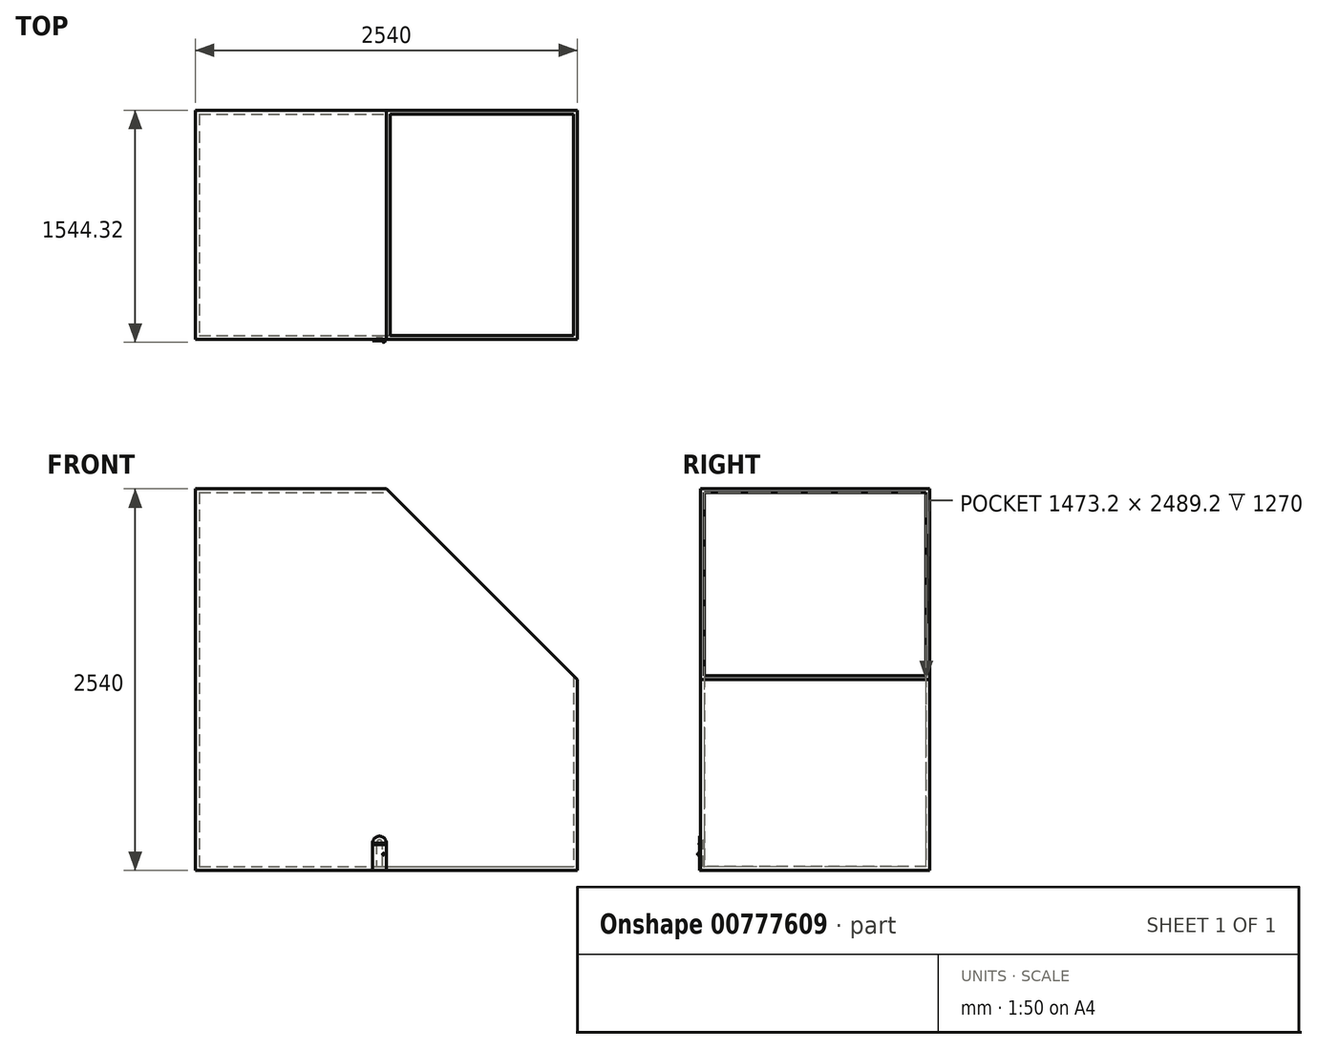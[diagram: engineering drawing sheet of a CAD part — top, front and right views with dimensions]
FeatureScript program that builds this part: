
annotation { "Feature Type Name" : "Feature", "Feature Type Description" : "" }
export const myFeature = defineFeature(function(context is Context, id is Id, definition is map)
    precondition{}
    {
        {
            var Q0;
            Q0=qCreatedBy(makeId("Top.planeOp"),FACE);
            var sketch = newSketch(context, id + "F0", { "sketchPlane" : qUnion([Q0])});
            skLineSegment(sketch, "E0.bottom", {"start": v(-1145.39, 766.67) * mm, "end": v(1394.61, 766.67) * mm});
            skLineSegment(sketch, "E0.top", {"start": v(-1145.39, -757.33) * mm, "end": v(1394.61, -757.33) * mm});
            skLineSegment(sketch, "E0.left", {"start": v(-1145.39, 766.67) * mm, "end": v(-1145.39, -757.33) * mm});
            skLineSegment(sketch, "E0.right", {"start": v(1394.61, 766.67) * mm, "end": v(1394.61, -757.33) * mm});
            skSolve(sketch);
        }
        {
            var Q0;
            Q0 = qSketchRegion(id + "F0", true);
            extrude(context, id + "F1", {"entities" : qUnion([Q0]), "depth" : 2540 * mm, "offsetDistance" : 25.4 * mm});
        }
        {
            var Q0;
            Q0=makeQuery(id+"F1.opExtrude","SWEPT_FACE",FACE,{"disambiguationData":[OSD([sQuery(id+"F0.wireOp",EDGE,"E0.top")])]});
            var sketch = newSketch(context, id + "F2", { "sketchPlane" : qUnion([Q0])});
            skLineSegment(sketch, "E1", {"start": v(124.61, 2540) * mm, "end": v(-1145.39, 1270) * mm});
            skLineSegment(sketch, "E2", {"start": v(-1145.39, 1270) * mm, "end": v(124.61, 2540) * mm});
            skLineSegment(sketch, "E3", {"start": v(124.61, 2540) * mm, "end": v(1394.61, 1270) * mm});
            skSolve(sketch);
        }
        {
            var Q0;
            Q0 = qSketchRegion(id + "F2", true);
            var Q1;
            {var subQ0=sQuery(id+"F2.wireOp",EDGE,"E2");Q1=makeQuery(id+"F2.imprint","IMPRINT",FACE,{"disambiguationData":[TD([[makeQuery(id+"F2.imprint","IMPRINT",EDGE,{"derivedFrom":subQ0}),1.0]])]});}
            var Q2;
            {var subQ0=sQuery(id+"F2.wireOp",EDGE,"E3");Q2=makeQuery(id+"F2.imprint","IMPRINT",FACE,{"disambiguationData":[TD([[makeQuery(id+"F2.imprint","IMPRINT",EDGE,{"derivedFrom":subQ0}),1.0]])]});}
            extrude(context, id + "F3", {"entities" : qUnion([Q0, Q1, Q2]), "operationType" : NewBodyOperationType.REMOVE, "oppositeDirection" : true, "depth" : 2540 * mm, "offsetDistance" : 25.4 * mm});
        }
        {
            var Q0;
            Q0=makeQuery(id+"F1.opExtrude","SWEPT_FACE",FACE,{"disambiguationData":[OSD([sQuery(id+"F0.wireOp",EDGE,"E0.top")])]});
            var sketch = newSketch(context, id + "F4", { "sketchPlane" : qUnion([Q0])});
            skLineSegment(sketch, "E4", {"start": v(1394.61, 0) * mm, "end": v(124.61, 0) * mm});
            skLineSegment(sketch, "E5", {"start": v(124.61, 0) * mm, "end": v(124.61, 182.88) * mm});
            skLineSegment(sketch, "E6", {"start": v(124.61, 182.88) * mm, "end": v(33.17, 182.88) * mm});
            skLineSegment(sketch, "E7", {"start": v(33.17, 182.88) * mm, "end": v(33.17, 0) * mm});
            skArc(sketch, "E8", {"start": v(124.61, 182.88) * mm, "mid": v(78.9, 228.6) * mm, "end": v(33.17, 182.88) * mm});
            skSolve(sketch);
        }
        {
            var Q0;
            Q0 = qSketchRegion(id + "F4", true);
            var Q1;
            {var subQ0=sQuery(id+"F4.wireOp",EDGE,"E5");Q1=makeQuery(id+"F4.imprint","IMPRINT",FACE,{"disambiguationData":[TD([[makeQuery(id+"F4.imprint","IMPRINT",EDGE,{"derivedFrom":subQ0}),1.0]])]});}
            extrude(context, id + "F5", {"entities" : qUnion([Q0, Q1]), "operationType" : NewBodyOperationType.ADD, "depth" : 7.62 * mm, "offsetDistance" : 25.4 * mm});
        }
        {
            var Q0;
            Q0=makeQuery(id+"F5.opExtrude","CAP_FACE",FACE,{"disambiguationData":[OSD([sQuery(id+"F0.wireOp",EDGE,"E0.top"),sQuery(id+"F4.wireOp",EDGE,"E5"),sQuery(id+"F4.wireOp",EDGE,"E7"),sQuery(id+"F4.wireOp",EDGE,"E8")])],"isStart":false});
            var sketch = newSketch(context, id + "F6", { "sketchPlane" : qUnion([Q0])});
            skLineSegment(sketch, "E9", {"start": v(33.17, 182.88) * mm, "end": v(124.61, 182.88) * mm});
            skLineSegment(sketch, "E10", {"start": v(124.61, 182.88) * mm, "end": v(124.61, 173.1) * mm});
            skLineSegment(sketch, "E11", {"start": v(124.61, 173.1) * mm, "end": v(33.17, 173.1) * mm});
            skLineSegment(sketch, "E12", {"start": v(33.17, 173.1) * mm, "end": v(33.17, 182.88) * mm});
            skSolve(sketch);
        }
        {
            var Q0;
            Q0 = qSketchRegion(id + "F6", true);
            extrude(context, id + "F7", {"entities" : qUnion([Q0]), "operationType" : NewBodyOperationType.ADD, "depth" : 2.54 * mm, "offsetDistance" : 25.4 * mm});
        }
        {
            var Q0;
            {var subQ0=sQuery(id+"F4.wireOp",EDGE,"E7");var subQ1=sQuery(id+"F0.wireOp",EDGE,"E0.top");var subQ2=sQuery(id+"F4.wireOp",EDGE,"E5");Q0=makeQuery(id+"F7.boolean.opBoolean","SPLIT",FACE,{"disambiguationData":[TD([makeQuery(id+"F5.opExtrude","SWEPT_FACE",FACE,{"disambiguationData":[OSD([subQ1])]})])],"derivedFrom":makeQuery(id+"F5.opExtrude","CAP_FACE",FACE,{"disambiguationData":[OSD([subQ1,subQ2,subQ0,sQuery(id+"F4.wireOp",EDGE,"E8")])],"isStart":false})});}
            var sketch = newSketch(context, id + "F8", { "sketchPlane" : qUnion([Q0])});
            skCircle(sketch, "E13", {"center": v(106.12, 108.6) * mm, "radius": 6.35 * mm});
            skSolve(sketch);
        }
        {
            var Q0;
            Q0 = qSketchRegion(id + "F8", true);
            extrude(context, id + "F9", {"entities" : qUnion([Q0]), "operationType" : NewBodyOperationType.ADD, "depth" : 12.7 * mm, "offsetDistance" : 25.4 * mm});
        }
        {
            var Q0;
            Q0=makeQuery(id+"F9.opExtrude","CAP_FACE",FACE,{"disambiguationData":[OSD([sQuery(id+"F8.wireOp",EDGE,"E13")])],"isStart":false});
            fillet(context, id + "F10", {"entities" : qUnion([Q0]), "radius" : 5.08 * mm, "tangentPropagation" : true, "allowEdgeOverflow" : false});
        }
        {
            var Q0;
            Q0=makeQuery(id+"F3.boolean.opBoolean","COPY",FACE,{"derivedFrom":makeQuery(id+"F3.opExtrude","SWEPT_FACE",FACE,{"disambiguationData":[OSD([sQuery(id+"F2.wireOp",EDGE,"E3")])]})});
            shell(context, id + "F11", {"entities" : qUnion([Q0]), "thickness" : 25.4 * mm});
        }
    });
